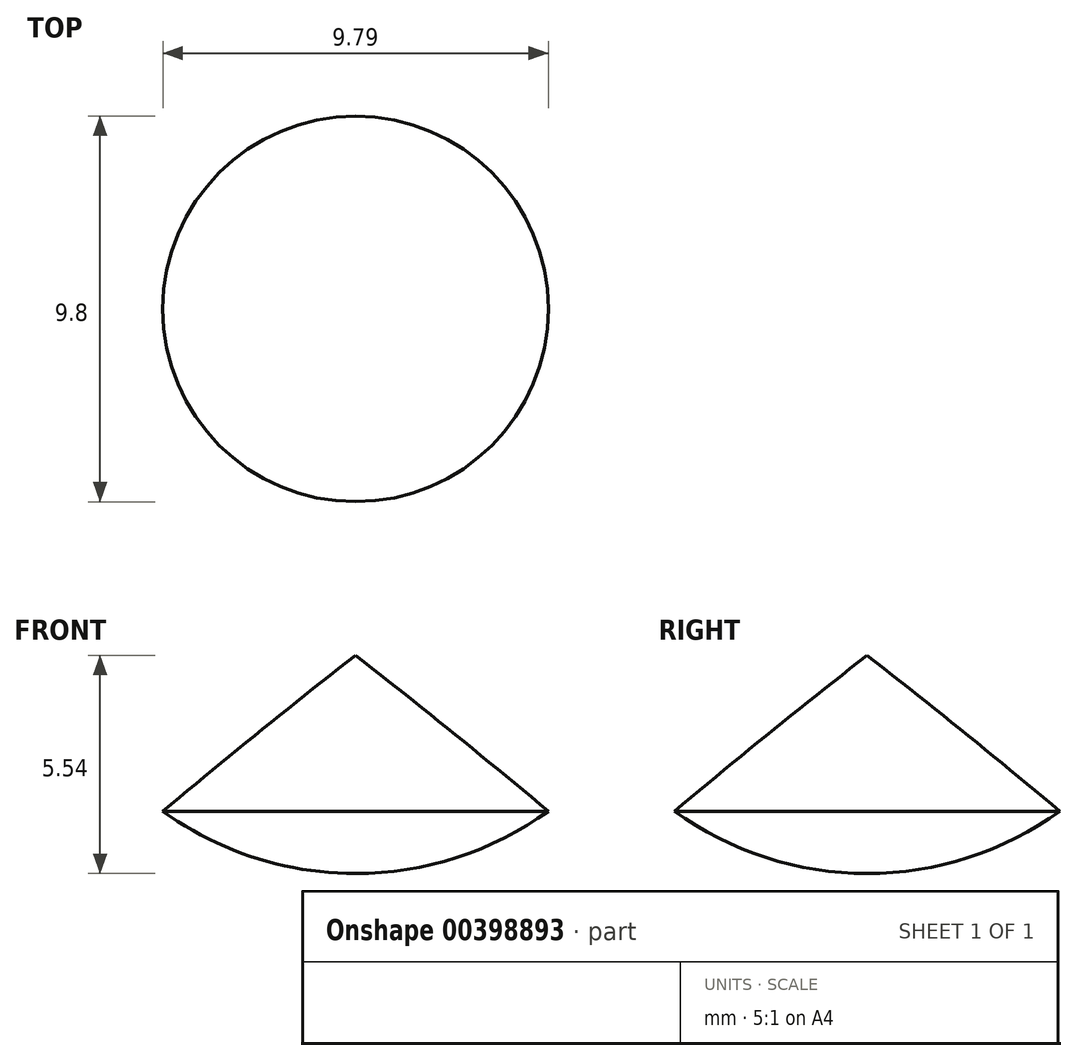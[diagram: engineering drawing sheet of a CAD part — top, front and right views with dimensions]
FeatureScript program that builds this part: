
annotation { "Feature Type Name" : "Feature", "Feature Type Description" : "" }
export const myFeature = defineFeature(function(context is Context, id is Id, definition is map)
    precondition{}
    {
        {
            var Q0;
            Q0=qCreatedBy(makeId("Front.planeOp"),FACE);
            var sketch = newSketch(context, id + "F0", { "sketchPlane" : qUnion([Q0])});
            skLineSegment(sketch, "E0", {"start": v(-18.47, 48.07) * mm, "end": v(-18.47, -61.53) * mm});
            skLineSegment(sketch, "E1", {"start": v(-18.47, -61.53) * mm, "end": v(27.43, -62.31) * mm});
            skFitSpline(sketch, "E2", {"points": [v(27.43, -62.31) * mm, v(68.7, -55.87) * mm, v(60.98, -31.38) * mm, v(27.67, -31.96) * mm, v(32.79, -20.5) * mm, v(-18.47, 48.07) * mm], "startDerivative": vector(114.91, 26.03) * mm, "endDerivative": vector(-229.6, 179.27) * mm});
            skCircle(sketch, "E3", {"center": v(-18.47, 50.9) * mm, "radius": 8.37 * mm});
            skSolve(sketch);
        }
        {
            var Q0;
            Q0=makeQuery(id+"F0.imprint","IMPRINT",FACE,{"disambiguationData":[TD([[makeQuery(id+"F0.imprint","IMPRINT",EDGE,{"derivedFrom":sQuery(id+"F0.wireOp",EDGE,"E0")}),1.0]])]});
            var Q1;
            Q1=sQuery(id+"F0.wireOp",EDGE,"E0");
            revolve(context, id + "F1", {"entities" : qUnion([Q0]), "axis" : qUnion([Q1]), "revolveType" : RevolveType.FULL});
        }
    });
